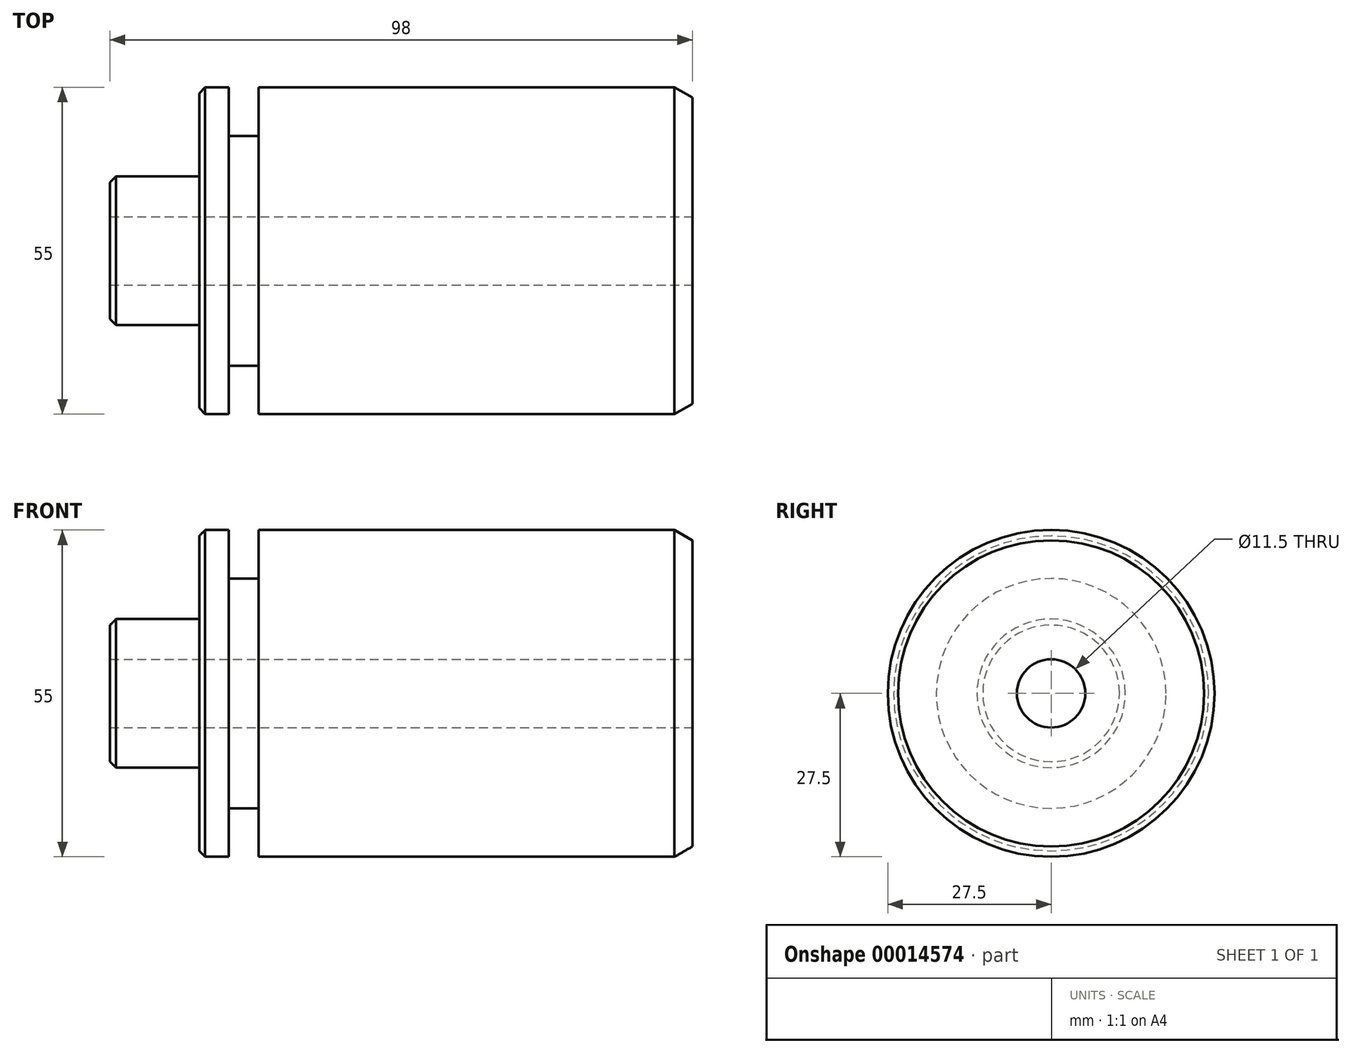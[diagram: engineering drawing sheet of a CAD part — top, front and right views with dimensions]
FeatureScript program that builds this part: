
annotation { "Feature Type Name" : "Feature", "Feature Type Description" : "" }
export const myFeature = defineFeature(function(context is Context, id is Id, definition is map)
    precondition{}
    {
        {
            var Q0;
            Q0=qCreatedBy(makeId("Front.planeOp"),FACE);
            var sketch = newSketch(context, id + "F0", { "sketchPlane" : qUnion([Q0])});
            skLineSegment(sketch, "E0", {"start": v(-135.9, 0) * mm, "end": v(158.07, 0) * mm, "construction": true});
            skLineSegment(sketch, "E1", {"start": v(0, 99.8) * mm, "end": v(0, -101.57) * mm, "construction": true});
            skLineSegment(sketch, "E2.0", {"start": v(-49, 99.8) * mm, "end": v(-49, -101.57) * mm, "construction": true});
            skLineSegment(sketch, "E3", {"start": v(-49, 0) * mm, "end": v(-49, 12.5) * mm});
            skLineSegment(sketch, "E4", {"start": v(-49, 12.5) * mm, "end": v(-34, 12.5) * mm});
            skLineSegment(sketch, "E5", {"start": v(-34, 12.5) * mm, "end": v(-34, 27.5) * mm});
            skLineSegment(sketch, "E6", {"start": v(-34, 27.5) * mm, "end": v(-29, 27.5) * mm});
            skLineSegment(sketch, "E7", {"start": v(-29, 27.5) * mm, "end": v(-29, 19.34) * mm});
            skLineSegment(sketch, "E8", {"start": v(-29, 19.34) * mm, "end": v(-24, 19.34) * mm});
            skLineSegment(sketch, "E9", {"start": v(-24, 19.34) * mm, "end": v(-24, 27.5) * mm});
            skLineSegment(sketch, "E10", {"start": v(-24, 27.5) * mm, "end": v(49, 27.5) * mm});
            skLineSegment(sketch, "E11", {"start": v(49, 27.5) * mm, "end": v(49, 0) * mm});
            skLineSegment(sketch, "E12", {"start": v(-49, 0) * mm, "end": v(49, 0) * mm});
            skSolve(sketch);
        }
        {
            var Q0;
            Q0=qSketchRegion(id+"F0",true);
            var Q1;
            Q1=sQuery(id+"F0.wireOp",EDGE,"E0");
            revolve(context, id + "F1", {"entities" : qUnion([Q0]), "axis" : qUnion([Q1]), "revolveType" : RevolveType.FULL});
        }
        {
            var Q0;
            Q0=makeQuery(id+"F1.opRevolve","SWEPT_FACE",FACE,{"disambiguationData":[OSD([sQuery(id+"F0.wireOp",EDGE,"E11")])]});
            var sketch = newSketch(context, id + "F2", { "sketchPlane" : qUnion([Q0])});
            skCircle(sketch, "E13", {"center": v(0, 0) * mm, "radius": 5.75 * mm});
            skSolve(sketch);
        }
        {
            var Q0;
            Q0=qSketchRegion(id+"F2",true);
            extrude(context, id + "F3", {"entities" : qUnion([Q0]), "operationType" : NewBodyOperationType.REMOVE, "endBound" : BoundingType.THROUGH_ALL, "oppositeDirection" : true, "depth" : 25 * mm});
        }
        {
            var Q0;
            Q0=makeQuery(id+"F1.opRevolve","SWEPT_EDGE",EDGE,{"disambiguationData":[OSD([sQuery(id+"F0.wireOp",EDGE,"E10"),sQuery(id+"F0.wireOp",EDGE,"E11")])]});
            chamfer(context, id + "F4", {"entities" : qUnion([Q0]), "chamferType" : ChamferType.OFFSET_ANGLE, "width" : 3 * mm, "oppositeDirection" : false, "angle" : 30 * degree, "tangentPropagation" : true});
        }
        {
            var Q0;
            Q0=makeQuery(id+"F1.opRevolve","SWEPT_EDGE",EDGE,{"disambiguationData":[OSD([sQuery(id+"F0.wireOp",EDGE,"E5"),sQuery(id+"F0.wireOp",EDGE,"E6")])]});
            chamfer(context, id + "F5", {"entities" : qUnion([Q0]), "width" : 1 * mm, "tangentPropagation" : true});
        }
        {
            var Q0;
            Q0=makeQuery(id+"F1.opRevolve","SWEPT_EDGE",EDGE,{"disambiguationData":[OSD([sQuery(id+"F0.wireOp",EDGE,"E3"),sQuery(id+"F0.wireOp",EDGE,"E4")])]});
            chamfer(context, id + "F6", {"entities" : qUnion([Q0]), "width" : 1 * mm, "tangentPropagation" : true});
        }
    });
